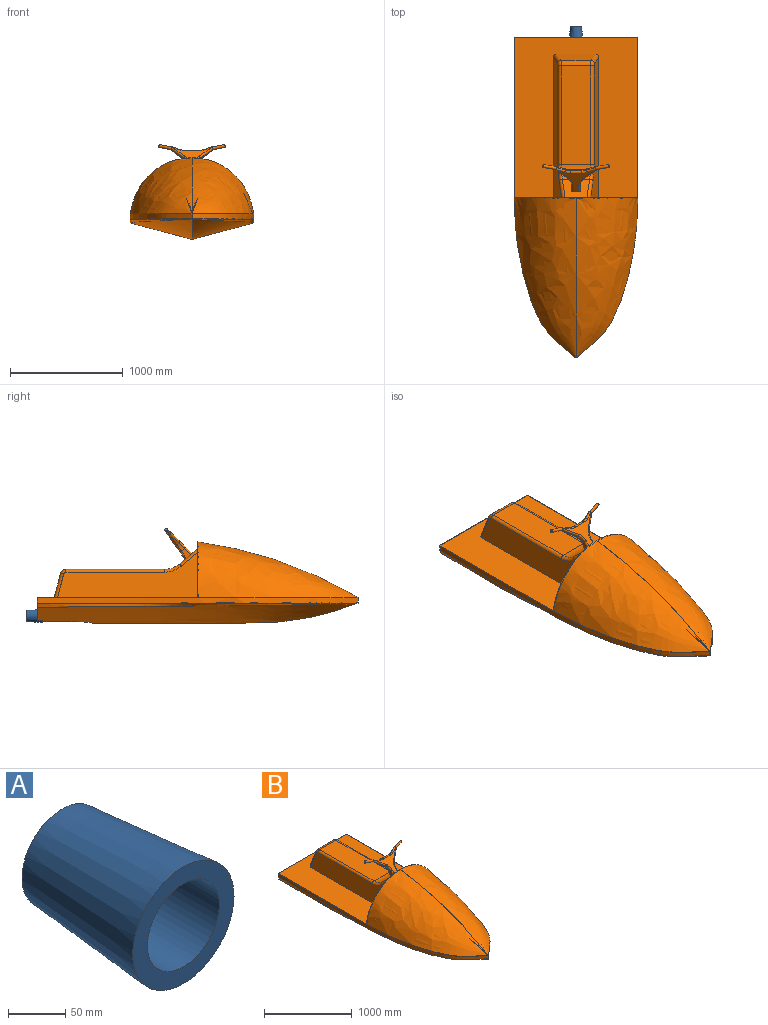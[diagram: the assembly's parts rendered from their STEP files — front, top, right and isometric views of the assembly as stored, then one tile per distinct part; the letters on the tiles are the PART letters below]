
ASSEMBLY  parts=2 mates=1
PART A: 4 faces, bbox 125x150x125 mm
  f0: cone r=62.5mm half-angle=5deg, axis (0,-1,0), area 52922mm2, adj f2,f3
  f1: cylinder r=44.38mm len=150mm, axis (0,-1,0), area 41824.1mm2, adj f2,f3
  f2: plane 125x125mm, normal (0,-1,0), area 6085.1mm2, adj f0,f1
  f3: plane 98.75x98.75mm, normal (0,1,0), area 1472.7mm2, adj f0,f1
PART B: 119 faces, bbox 1499.1x2877.5x928.9 mm
  f0: cylinder r=12.5mm len=122.38mm, axis (0.97,-0.17,-0.2), area 9424.8mm2, adj f62,f79
  f1: cylinder r=15mm len=127.75mm, axis (0.71,-0.41,-0.58), area 3949.3mm2, adj f34,f56,f58,f63,f79
  f2: cylinder r=15mm len=127.75mm, axis (-0.71,-0.41,-0.58), area 3949.3mm2, adj f6,f34,f37,f42,f44
  f3: cylinder r=15mm len=106.38mm, axis (1,0,0), area 2367.3mm2, adj f34,f35,f43,f57
  f4: cylinder r=12.5mm len=122.38mm, axis (-0.97,-0.17,-0.2), area 9424.8mm2, adj f6,f38
  f5: cylinder r=62.5mm len=125mm, axis (0,1,0), area 19635mm2, adj f28,f30,f31,f66
  f6: plane 34.43x34.17mm, normal (0.97,0.17,0.2), area 252.9mm2, adj f2,f4,f36,f37,f44,f48,f50
  f7: plane 243.07x164.88mm, normal (0,0.64,0.77), area 40601mm2, adj f10,f18,f24,f32,f33,f34,f41,f45
  f8: bspline ~2850x549.31mm, area 1236965.8mm2, adj f11,f12,f25,f28,f29,f31,f78
  f9: plane 1430.22x1105.22mm, normal (0,0,1), area 1057864.9mm2, adj f10,f11,f13,f15,f17,f20,f73,f74
  f10: plane 1108.64x503.32mm, normal (0,1,0), area 273721.9mm2, adj f7,f9,f14,f17,f24,f69,f74,f75
  f11: plane 1100x203.21mm, normal (0,1,0), area 138581.8mm2, adj f8,f9,f12,f13,f25,f26,f27,f67
  f12: bspline ~2850x550mm, area 191951.9mm2, adj f8,f11,f13
  f13: extruded ~2850x550mm, area 150753.1mm2, adj f9,f11,f12,f14,f76
  f14: bspline ~1425x550mm, area 581527mm2, adj f10,f13,f75
  f15: plane 341.81x212.94mm, normal (0,0.97,0.26), area 67076.1mm2, adj f9,f19,f20,f73
  f16: plane 876.76x261.49mm, normal (0,0,1), area 229264.9mm2, adj f18,f19,f22,f71
  f17: plane 1245.97x401.36mm, normal (0.98,0,0.17), area 297282.8mm2, adj f9,f10,f20,f21,f22,f23,f24
  f18: cylinder r=200mm len=261.49mm, axis (1,0,0), area 35186.2mm2, adj f7,f16,f23,f70
  f19: cylinder r=50mm len=266.72mm, axis (-1,0,0), area 17285.6mm2, adj f15,f16,f21,f72
  f20: cylinder r=30mm len=216.89mm, axis (0.17,0.26,-0.95), area 10175.2mm2, adj f9,f15,f17,f21
  f21: bspline ~48.3x39.61mm, area 2169.6mm2, adj f17,f19,f20,f22
  f22: cylinder r=30mm len=876.76mm, axis (0,1,0), area 36725.7mm2, adj f16,f17,f21,f23
  f23: bspline ~147.84x73.48mm, area 6275.2mm2, adj f17,f18,f22,f24
  f24: cylinder r=30mm len=183.61mm, axis (0.11,0.76,-0.64), area 8763.1mm2, adj f7,f10,f17,f23
  f25: plane 123.23x50.01mm, normal (-1,0,0), area 6160.5mm2, adj f8,f11,f26,f28
  f26: cylinder r=30mm len=50mm, axis (0,1,0), area 2356.2mm2, adj f11,f25,f27,f28
  f27: plane 140x50mm, normal (0,0,-1), area 7000mm2, adj f11,f26,f28,f67
  f28: plane 200x163.26mm, normal (0,1,0), area 19408.2mm2, adj f5,f8,f25,f26,f27,f31,f66,f67
  f29: cylinder r=62.5mm len=296.79mm, axis (0,-0.92,-0.39), area 39186.6mm2, adj f8,f30,f31,f66,f78
  f30: torus R=137.5mm, axis (1,0,0), area 13833.4mm2, adj f5,f29,f31,f66
  f31: plane 248.88x50.99mm, normal (-1,0,0), area 9503.6mm2, adj f5,f8,f28,f29,f30
  f32: plane 343.39x194.93mm, normal (0,-0.71,0.71), area 25247.3mm2, adj f7,f45,f46,f47,f48,f49,f50,f51
  f33: plane 87.84x83.46mm, normal (1,0,0), area 3379.7mm2, adj f7,f40,f41,f45
  f34: plane 343.39x225.75mm, normal (0,0.82,-0.57), area 25247.3mm2, adj f1,f2,f3,f7,f41,f42,f43,f44
  f35: plane 106.38x7.39mm, normal (0,0.64,0.77), area 1025.6mm2, adj f3,f39,f47,f61
  f36: plane 78.43x30.52mm, normal (-0.42,0.58,0.7), area 402.9mm2, adj f6,f39,f44,f50
  f37: plane 111.73x93.39mm, normal (0.71,-0.45,-0.54), area 1917mm2, adj f2,f6,f40,f48
  f38: plane 24.65x24.5mm, normal (0.97,0.17,0.2), area 490.9mm2, adj f4
  f39: cylinder r=100mm len=41.64mm, axis (0,0.77,-0.64), area 374.8mm2, adj f35,f36,f43,f49
  f40: cylinder r=100mm len=77.4mm, axis (0,0.77,-0.64), area 2279.3mm2, adj f33,f37,f42,f46
  f41: cylinder r=15mm len=74.29mm, axis (0,0.57,0.82), area 1874mm2, adj f7,f33,f34,f42
  f42: bspline ~67.34x59.11mm, area 1996.9mm2, adj f2,f34,f40,f41
  f43: bspline ~47.88x27.64mm, area 1012.5mm2, adj f3,f34,f39,f44
  f44: cylinder r=15mm len=84.67mm, axis (0.91,0.24,0.34), area 1896.1mm2, adj f2,f6,f34,f36,f43
  f45: cylinder r=15mm len=67.31mm, axis (0,0.71,0.71), area 1874mm2, adj f7,f32,f33,f46
  f46: bspline ~68.33x61.51mm, area 1996.9mm2, adj f32,f40,f45,f48
  f47: cylinder r=15mm len=106.38mm, axis (-1,0,0), area 2367.3mm2, adj f32,f35,f49,f52
  f48: cylinder r=15mm len=127.75mm, axis (0.71,0.5,0.5), area 3971.1mm2, adj f6,f32,f37,f46,f50
  f49: bspline ~47.88x26.79mm, area 1012.5mm2, adj f32,f39,f47,f50
  f50: cylinder r=15mm len=84.67mm, axis (-0.91,-0.3,-0.3), area 1896.1mm2, adj f6,f32,f36,f48,f49
  f51: cylinder r=15mm len=84.67mm, axis (0.91,-0.3,-0.3), area 1896.1mm2, adj f32,f52,f53,f64,f79
  f52: bspline ~47.88x26.79mm, area 1012.5mm2, adj f32,f47,f51,f61
  f53: cylinder r=15mm len=127.75mm, axis (-0.71,0.5,0.5), area 3971.1mm2, adj f32,f51,f54,f63,f79
  f54: bspline ~68.33x61.51mm, area 1996.9mm2, adj f32,f53,f55,f60
  f55: cylinder r=15mm len=67.31mm, axis (0,0.71,0.71), area 1874mm2, adj f7,f32,f54,f65
  f56: cylinder r=15mm len=84.67mm, axis (-0.91,0.24,0.34), area 1896.1mm2, adj f1,f34,f57,f64,f79
  f57: bspline ~47.88x27.64mm, area 1012.5mm2, adj f3,f34,f56,f61
  f58: bspline ~67.34x59.11mm, area 1996.9mm2, adj f1,f34,f59,f60
  f59: cylinder r=15mm len=74.29mm, axis (0,0.57,0.82), area 1874mm2, adj f7,f34,f58,f65
  f60: cylinder r=100mm len=77.4mm, axis (0,0.77,-0.64), area 2279.3mm2, adj f54,f58,f63,f65
  f61: cylinder r=100mm len=41.64mm, axis (0,0.77,-0.64), area 374.8mm2, adj f35,f52,f57,f64
  f62: plane 24.65x24.5mm, normal (-0.97,0.17,0.2), area 490.9mm2, adj f0
  f63: plane 111.73x93.39mm, normal (-0.71,-0.45,-0.54), area 1917mm2, adj f1,f53,f60,f79
  f64: plane 78.43x30.52mm, normal (0.42,0.58,0.7), area 402.9mm2, adj f51,f56,f61,f79
  f65: plane 87.84x83.46mm, normal (-1,0,0), area 3379.7mm2, adj f7,f55,f59,f60
  f66: plane 248.88x50.99mm, normal (1,0,0), area 9503.6mm2, adj f5,f28,f29,f30,f78
  f67: cylinder r=30mm len=50mm, axis (0,1,0), area 2356.2mm2, adj f11,f27,f28,f68
  f68: plane 123.23x50.01mm, normal (1,0,0), area 6160.5mm2, adj f11,f28,f67,f78
  f69: cylinder r=30mm len=183.61mm, axis (-0.11,0.76,-0.64), area 8763.1mm2, adj f7,f10,f70,f74
  f70: bspline ~147.84x73.48mm, area 6275.2mm2, adj f18,f69,f71,f74
  f71: cylinder r=30mm len=876.76mm, axis (0,1,0), area 36725.7mm2, adj f16,f70,f72,f74
  f72: bspline ~48.3x39.61mm, area 2169.6mm2, adj f19,f71,f73,f74
  f73: cylinder r=30mm len=216.89mm, axis (-0.17,0.26,-0.95), area 10175.2mm2, adj f9,f15,f72,f74
  f74: plane 1245.97x401.36mm, normal (-0.98,0,0.17), area 297282.8mm2, adj f9,f10,f69,f70,f71,f72,f73
  f75: bspline ~1425x550mm, area 494940.4mm2, adj f10,f14,f76
  f76: extruded ~2850x550mm, area 150753.1mm2, adj f9,f11,f13,f75,f77
  f77: bspline ~2850x550mm, area 191951.9mm2, adj f11,f76,f78
  f78: bspline ~2850x549.31mm, area 1236975.2mm2, adj f8,f11,f28,f29,f66,f68,f77
  f79: plane 34.43x34.17mm, normal (-0.97,0.17,0.2), area 252.9mm2, adj f0,f1,f51,f53,f56,f63,f64
  f80: cylinder r=67.5mm len=135mm, axis (0,1,0), area 20145.5mm2, adj f93,f103,f109,f111
  f81: bspline ~2848.51x738.61mm, area 1216956.4mm2, adj f82,f83,f91,f93,f110,f111,f115,f118
  f82: bspline ~2849.81x547.7mm, area 196430.5mm2, adj f81,f83,f115
  f83: extruded ~2838.56x545mm, area 133679.2mm2, adj f81,f82,f84,f114,f115,f116,f117
  f84: bspline ~1420.4x545.5mm, area 487597.6mm2, adj f83,f113,f116
  f85: plane 1252.08x409.68mm, normal (0.98,0,-0.17), area 304576.1mm2, adj f86,f87,f88,f89,f90,f116,f117
  f86: cylinder r=25mm len=219.94mm, axis (-0.17,0.26,-0.95), area 8636.3mm2, adj f85,f87,f108,f117
  f87: bspline ~43.47x35.48mm, area 1665mm2, adj f85,f86,f88,f104
  f88: cylinder r=25mm len=876.76mm, axis (0,1,0), area 30604.8mm2, adj f85,f87,f89,f107
  f89: bspline ~147.84x70.2mm, area 5303.5mm2, adj f85,f88,f90,f105
  f90: cylinder r=25mm len=182.18mm, axis (-0.11,0.76,-0.64), area 7462.8mm2, adj f85,f89,f106,f116
  f91: plane 116.71x50.01mm, normal (-1,0,0), area 5834.8mm2, adj f81,f92,f111,f115
  f92: cylinder r=35mm len=50mm, axis (0,1,0), area 2748.9mm2, adj f91,f111,f112,f115
  f93: plane 228.31x44.43mm, normal (-1,0,0), area 7713.1mm2, adj f80,f81,f109,f110,f111
  f94: plane 1252.08x409.68mm, normal (-0.98,0,-0.17), area 304576.1mm2, adj f96,f97,f98,f99,f100,f116,f117
  f95: bspline ~2849.81x547.7mm, area 194218.1mm2, adj f114,f115,f118
  f96: cylinder r=25mm len=219.94mm, axis (0.17,0.26,-0.95), area 8636.3mm2, adj f94,f100,f108,f117
  f97: cylinder r=25mm len=876.76mm, axis (0,1,0), area 30604.8mm2, adj f94,f99,f100,f107
  f98: cylinder r=25mm len=182.18mm, axis (0.11,0.76,-0.64), area 7462.8mm2, adj f94,f99,f106,f116
  f99: bspline ~147.84x70.2mm, area 5303.5mm2, adj f94,f97,f98,f105
  f100: bspline ~43.47x35.48mm, area 1665mm2, adj f94,f96,f97,f104
  f101: cylinder r=35mm len=50mm, axis (0,1,0), area 2748.9mm2, adj f102,f111,f112,f115
  f102: plane 116.71x50.01mm, normal (1,0,0), area 5834.8mm2, adj f101,f111,f115,f118
  f103: plane 228.31x44.43mm, normal (1,0,0), area 7713.1mm2, adj f80,f109,f110,f111,f118
  f104: cylinder r=45mm len=266.72mm, axis (-1,0,0), area 15557mm2, adj f87,f100,f107,f108
  f105: cylinder r=205mm len=261.49mm, axis (1,0,0), area 36065.8mm2, adj f89,f99,f106,f107
  f106: plane 242.51x166.11mm, normal (0,-0.64,-0.77), area 47258.6mm2, adj f90,f98,f105,f116
  f107: plane 876.76x261.49mm, normal (0,0,-1), area 229264.9mm2, adj f88,f97,f104,f105
  f108: plane 343.12x216.65mm, normal (0,-0.97,-0.26), area 68390mm2, adj f86,f96,f104,f117
  f109: torus R=137.5mm, axis (1,0,0), area 15208.3mm2, adj f80,f93,f103,f110
  f110: cylinder r=67.5mm len=297.37mm, axis (0,-0.92,-0.39), area 40381.9mm2, adj f81,f93,f103,f109,f118
  f111: plane 210x161.75mm, normal (0,-1,0), area 19934.1mm2, adj f80,f81,f91,f92,f93,f101,f102,f103
  f112: plane 140x50mm, normal (0,0,1), area 7000mm2, adj f92,f101,f111,f115
  f113: bspline ~1420.4x545.5mm, area 487597.6mm2, adj f84,f114,f116
  f114: extruded ~2838.56x545mm, area 133301.4mm2, adj f83,f95,f113,f115,f116,f117,f118
  f115: plane 1090.01x191.7mm, normal (0,-1,0), area 125389.2mm2, adj f81,f82,f83,f91,f92,f95,f101,f102
  f116: plane 1117.51x521.46mm, normal (0,-1,0), area 273177.3mm2, adj f83,f84,f85,f90,f94,f98,f106,f113
  f117: plane 1429.35x1094.36mm, normal (0,0,-1), area 1053741.5mm2, adj f83,f85,f86,f94,f96,f108,f114,f115
  f118: bspline ~2848.51x738.61mm, area 1227328.9mm2, adj f81,f95,f102,f103,f110,f111,f114,f115
PLACE A at identity
PLACE B at identity fixed
MATE fastened B.f5 <-> A.f0  axis (0,1,0) through (0,1375,-112.5)mm
